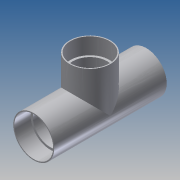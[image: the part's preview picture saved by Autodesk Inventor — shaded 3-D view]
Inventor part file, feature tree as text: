
AUTODESK INVENTOR PART (.ipt)
format: ipt  version: 2013 SP2 (Build 170200200, 200)  size: 201,728 bytes
history: native  units: in
note: dims shown in document units (in); Inventor stores cm internally (conversion verified against a paired STEP export)
features: sketch x8, extrude x7, plane x1
ambient origin geometry x8: Origin, YZ Plane, XZ Plane, XY Plane, X Axis, Y Axis, Z Axis, Center Point
bodies: Solid1 (feature_tree)
feature tree (16):
  extrude  "mainBody"  Depth=6.875in TaperAngle=0.0deg
  sketch  "Sketch10"  dims[d29=3.4375in d30=2.5in]
  plane  "Work Plane5"
  extrude  "TBody"  Depth=2.5in
  extrude  "TSocket"  Depth=2.375in
  extrude  "TTube"  Depth=2.1in
  extrude  "mainTube"  Depth=2.1in
  extrude  "mainSocket1"  Depth=2.375in
  extrude  "mainSocket2"  Depth=2.375in
  sketch  "Sketch1"  dims[d0=2.5in d1=6.875in d2=0.0in]
  sketch  "Sketch11"  dims[d31=1.5in d32=1.25in d33=0.0in d34=0.0in d35=2.375in]
  sketch  "Sketch12"  dims[d37=1.0in d38=0.0in d39=2.1in]
  sketch  "Sketch13"  dims[d41=1.5in d42=0.0in d43=2.1in]
  sketch  "Sketch14"  dims[d45=7.0in d46=0.0in d47=2.375in]
  sketch  "Sketch15"  dims[d49=1.0in d50=0.0in d51=2.375in]
  sketch  "Sketch16"  dims[d53=1.0in d54=0.0in]
